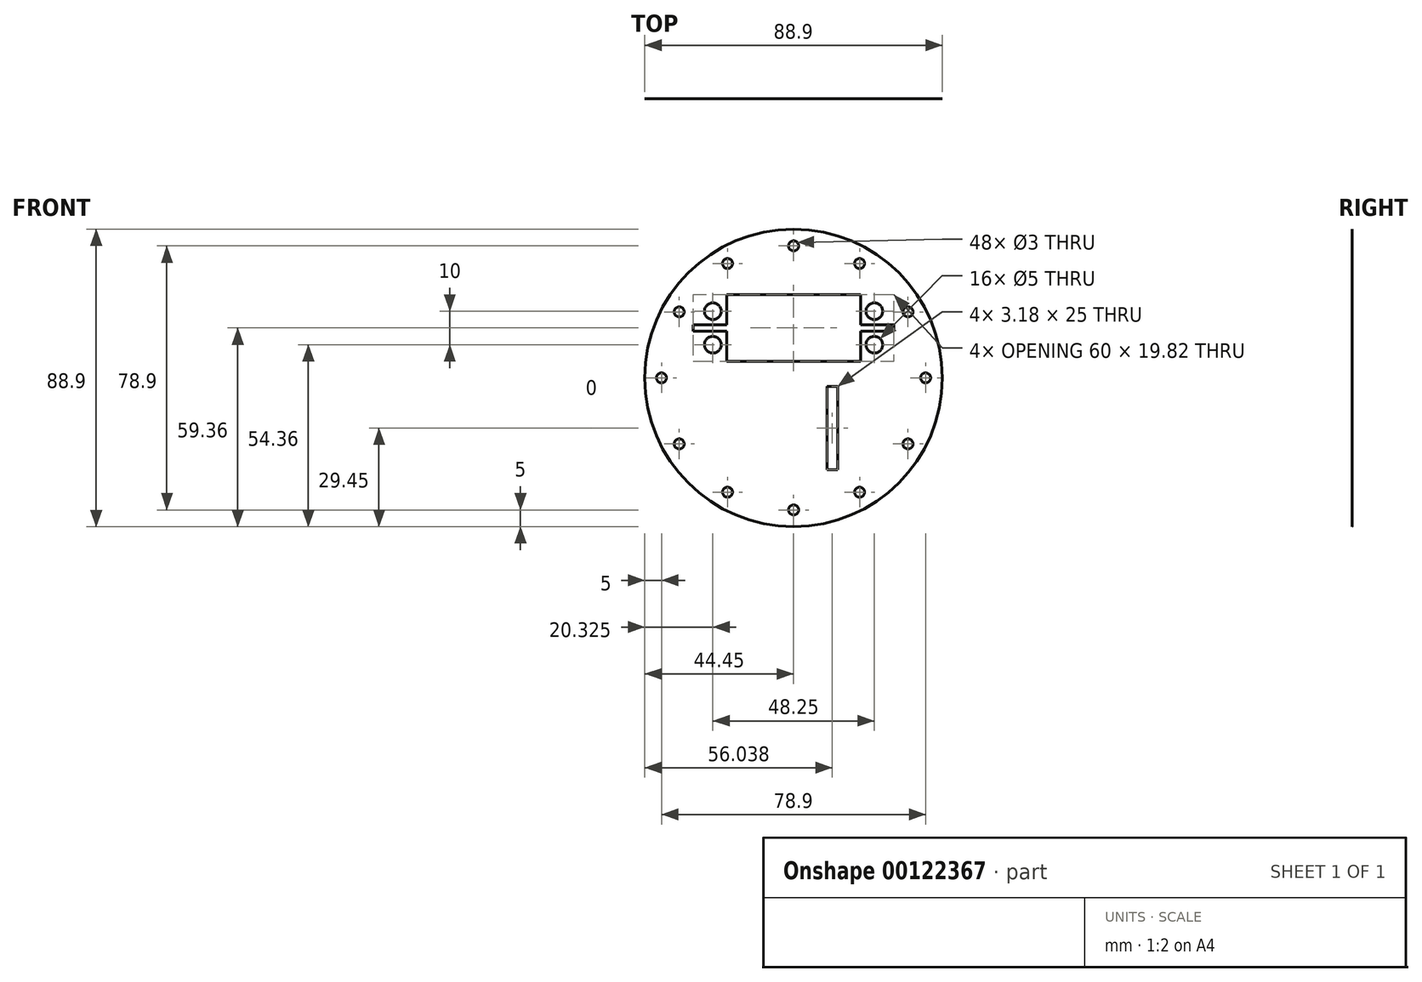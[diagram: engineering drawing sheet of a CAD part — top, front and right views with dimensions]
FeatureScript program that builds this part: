
annotation { "Feature Type Name" : "Feature", "Feature Type Description" : "" }
export const myFeature = defineFeature(function(context is Context, id is Id, definition is map)
    precondition{}
    {
        {
            var Q0;
            Q0=qCreatedBy(makeId("Front.planeOp"),FACE);
            var sketch = newSketch(context, id + "F0", { "sketchPlane" : qUnion([Q0])});
            skCircle(sketch, "E0", {"center": v(0, 0) * mm, "radius": 44.45 * mm});
            skLineSegment(sketch, "E1.bottom", {"start": v(-20, 24.82) * mm, "end": v(20, 24.82) * mm});
            skLineSegment(sketch, "E1.top", {"start": v(-20, 5) * mm, "end": v(20, 5) * mm});
            skLineSegment(sketch, "E1.left", {"start": v(-20, 24.82) * mm, "end": v(-20, 15.9) * mm});
            skLineSegment(sketch, "E1.right", {"start": v(20, 24.82) * mm, "end": v(20, 15.9) * mm});
            skCircle(sketch, "E2", {"center": v(24.12, 19.9) * mm, "radius": 2.5 * mm});
            skCircle(sketch, "E3", {"center": v(24.12, 9.91) * mm, "radius": 2.5 * mm});
            skCircle(sketch, "E4", {"center": v(-24.12, 19.9) * mm, "radius": 2.5 * mm});
            skCircle(sketch, "E5", {"center": v(-24.12, 9.9) * mm, "radius": 2.5 * mm});
            skPoint(sketch, "E6.end.orphan", {"position": v(20, 14.91) * mm});
            skPoint(sketch, "E6.start.orphan", {"position": v(-20, 14.9) * mm});
            skLineSegment(sketch, "E7", {"start": v(0, -15) * mm, "end": v(10, -15) * mm});
            skLineSegment(sketch, "E8.bottom", {"start": v(-20, 15.9) * mm, "end": v(-30, 15.9) * mm});
            skLineSegment(sketch, "E8.top", {"start": v(-20, 13.9) * mm, "end": v(-30, 13.9) * mm});
            skLineSegment(sketch, "E8.right", {"start": v(-30, 15.9) * mm, "end": v(-30, 13.9) * mm});
            skLineSegment(sketch, "E9.trimOffspring", {"start": v(20, 28.91) * mm, "end": v(20, 15.9) * mm});
            skLineSegment(sketch, "E10.trimOffspring", {"start": v(-20, 13.9) * mm, "end": v(-20, 5) * mm});
            skCircle(sketch, "E11", {"center": v(39.45, 0) * mm, "radius": 1.5 * mm});
            skCircle(sketch, "E12.1.0", {"center": v(34.16, 19.72) * mm, "radius": 1.5 * mm});
            skCircle(sketch, "E12.2.0", {"center": v(19.73, 34.16) * mm, "radius": 1.5 * mm});
            skCircle(sketch, "E12.3.0", {"center": v(0, 39.45) * mm, "radius": 1.5 * mm});
            skCircle(sketch, "E12.4.0", {"center": v(-19.72, 34.16) * mm, "radius": 1.5 * mm});
            skCircle(sketch, "E12.5.0", {"center": v(-34.16, 19.73) * mm, "radius": 1.5 * mm});
            skCircle(sketch, "E12.6.0", {"center": v(-39.45, 0) * mm, "radius": 1.5 * mm});
            skCircle(sketch, "E12.7.0", {"center": v(-34.16, -19.72) * mm, "radius": 1.5 * mm});
            skCircle(sketch, "E12.8.0", {"center": v(-19.73, -34.16) * mm, "radius": 1.5 * mm});
            skCircle(sketch, "E12.9.0", {"center": v(0, -39.45) * mm, "radius": 1.5 * mm});
            skCircle(sketch, "E12.10.0", {"center": v(19.72, -34.16) * mm, "radius": 1.5 * mm});
            skCircle(sketch, "E12.11.0", {"center": v(34.16, -19.72) * mm, "radius": 1.5 * mm});
            skLineSegment(sketch, "E13.bottom", {"start": v(20, 15.9) * mm, "end": v(30, 15.9) * mm});
            skLineSegment(sketch, "E13.top", {"start": v(20, 13.9) * mm, "end": v(30, 13.9) * mm});
            skLineSegment(sketch, "E13.right", {"start": v(30, 15.9) * mm, "end": v(30, 13.9) * mm});
            skLineSegment(sketch, "E14.trimOffspring", {"start": v(20, 13.9) * mm, "end": v(20, 5) * mm});
            skLineSegment(sketch, "E15.bottom", {"start": v(10, -15) * mm, "end": v(13.18, -15) * mm});
            skLineSegment(sketch, "E15.top", {"start": v(10, -2.5) * mm, "end": v(13.17, -2.5) * mm});
            skLineSegment(sketch, "E15.left", {"start": v(10, -15) * mm, "end": v(10, -2.5) * mm});
            skLineSegment(sketch, "E15.right", {"start": v(13.18, -15) * mm, "end": v(13.17, -2.5) * mm});
            skLineSegment(sketch, "E16.top", {"start": v(10, -27.5) * mm, "end": v(13.18, -27.5) * mm});
            skLineSegment(sketch, "E16.left", {"start": v(10, -15) * mm, "end": v(10, -27.5) * mm});
            skLineSegment(sketch, "E16.right", {"start": v(13.18, -15) * mm, "end": v(13.18, -27.5) * mm});
            skSolve(sketch);
        }
        {
            var Q0;
            Q0=makeQuery(id+"F0.imprint","IMPRINT",FACE,{"disambiguationData":[TD([[makeQuery(id+"F0.imprint","IMPRINT",EDGE,{"derivedFrom":sQuery(id+"F0.wireOp",EDGE,"E0")}),1.0]])]});
            extrude(context, id + "F1", {"entities" : qUnion([Q0]), "depth" : 1 / 203.2 * mm});
        }
    });
